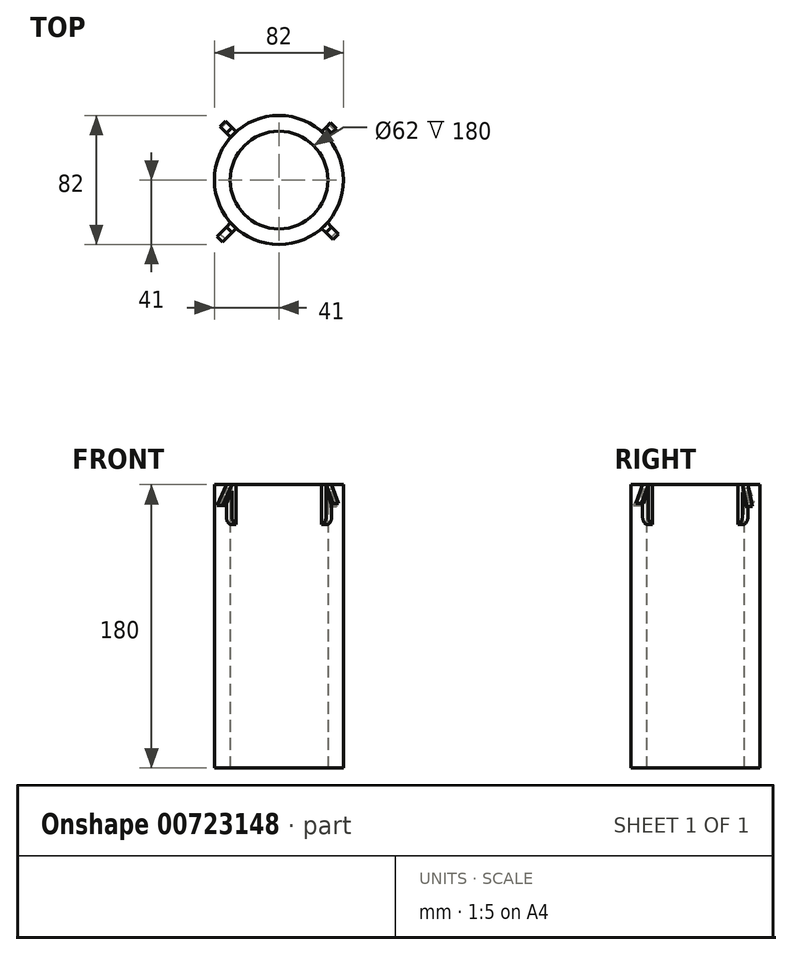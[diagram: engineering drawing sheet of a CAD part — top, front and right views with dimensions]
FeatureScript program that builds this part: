
annotation { "Feature Type Name" : "Feature", "Feature Type Description" : "" }
export const myFeature = defineFeature(function(context is Context, id is Id, definition is map)
    precondition{}
    {
        {
            var Q0;
            Q0=qCreatedBy(makeId("Top.planeOp"),FACE);
            var sketch = newSketch(context, id + "F0", { "sketchPlane" : qUnion([Q0])});
            skCircle(sketch, "E0", {"center": v(0, 0) * mm, "radius": 41 * mm});
            skCircle(sketch, "E1.0", {"center": v(0, 0) * mm, "radius": 31 * mm});
            skSolve(sketch);
        }
        {
            var Q0;
            Q0=makeQuery(id+"F0.imprint","IMPRINT",FACE,{"disambiguationData":[TD([[makeQuery(id+"F0.imprint","IMPRINT",EDGE,{"derivedFrom":sQuery(id+"F0.wireOp",EDGE,"E0")}),1.0]])]});
            extrude(context, id + "F1", {"entities" : qUnion([Q0]), "endBound" : BoundingType.SYMMETRIC, "depth" : 180 * mm, "offsetDistance" : 25.4 * mm});
        }
        {
            var Q0;
            Q0=makeQuery(id+"F1.opExtrude","CAP_FACE",FACE,{"disambiguationData":[OSD([sQuery(id+"F0.wireOp",EDGE,"E0"),sQuery(id+"F0.wireOp",EDGE,"E1.0")])],"isStart":false});
            var sketch = newSketch(context, id + "F2", { "sketchPlane" : qUnion([Q0])});
            skLineSegment(sketch, "E2", {"start": v(0, 77.1) * mm, "end": v(0, -58.5) * mm});
            skLineSegment(sketch, "E3", {"start": v(-76.39, 0) * mm, "end": v(76.39, 0) * mm});
            skLineSegment(sketch, "E4", {"start": v(-30.73, 27.14) * mm, "end": v(-33.43, 29.83) * mm});
            skLineSegment(sketch, "E5", {"start": v(-33.43, 29.83) * mm, "end": v(-31.63, 31.63) * mm});
            skLineSegment(sketch, "E6", {"start": v(-31.63, 31.63) * mm, "end": v(-29.83, 33.43) * mm});
            skLineSegment(sketch, "E7", {"start": v(-29.83, 33.43) * mm, "end": v(-27.14, 30.73) * mm});
            skPoint(sketch, "E8.MirrorCS.end.orphan", {"position": v(68.66, 68.66) * mm});
            skPoint(sketch, "E8.MirrorCS.start.orphan", {"position": v(0, 0) * mm});
            skLineSegment(sketch, "E9.MirrorCS", {"start": v(33.43, 29.83) * mm, "end": v(31.63, 31.63) * mm});
            skLineSegment(sketch, "E10.MirrorCS", {"start": v(30.73, 27.14) * mm, "end": v(33.43, 29.83) * mm});
            skLineSegment(sketch, "E11.MirrorCS", {"start": v(31.63, 31.63) * mm, "end": v(29.83, 33.43) * mm});
            skLineSegment(sketch, "E12.MirrorCS", {"start": v(29.83, 33.43) * mm, "end": v(27.14, 30.73) * mm});
            skLineSegment(sketch, "E13.MirrorCS", {"start": v(-30.73, -27.14) * mm, "end": v(-33.43, -29.83) * mm});
            skLineSegment(sketch, "E14.MirrorCS", {"start": v(-33.43, -29.83) * mm, "end": v(-31.63, -31.63) * mm});
            skLineSegment(sketch, "E15.MirrorCS", {"start": v(-31.63, -31.63) * mm, "end": v(-29.83, -33.43) * mm});
            skLineSegment(sketch, "E16.MirrorCS", {"start": v(-29.83, -33.43) * mm, "end": v(-27.14, -30.73) * mm});
            skLineSegment(sketch, "E17.MirrorCS", {"start": v(29.83, -33.43) * mm, "end": v(27.14, -30.73) * mm});
            skLineSegment(sketch, "E18.MirrorCS", {"start": v(31.63, -31.63) * mm, "end": v(29.83, -33.43) * mm});
            skLineSegment(sketch, "E19.MirrorCS", {"start": v(33.43, -29.83) * mm, "end": v(31.63, -31.63) * mm});
            skLineSegment(sketch, "E20.MirrorCS", {"start": v(30.73, -27.14) * mm, "end": v(33.43, -29.83) * mm});
            skSolve(sketch);
        }
        {
            var Q0;
            {var subQ1=sQuery(id+"F2.wireOp",EDGE,"E4");Q0=makeQuery(id+"F2.imprint","IMPRINT",FACE,{"disambiguationData":[TD([[makeQuery(id+"F2.imprint","IMPRINT",EDGE,{"derivedFrom":subQ1}),-1.0]])]});}
            var Q1;
            Q1=makeQuery(id+"F2.imprint","IMPRINT",FACE,{"disambiguationData":[TD([[makeQuery(id+"F2.imprint","IMPRINT",EDGE,{"derivedFrom":sQuery(id+"F2.wireOp",EDGE,"E9.MirrorCS")}),1.0]])]});
            var Q2;
            {var subQ1=sQuery(id+"F2.wireOp",EDGE,"E17.MirrorCS");Q2=makeQuery(id+"F2.imprint","IMPRINT",FACE,{"disambiguationData":[TD([[makeQuery(id+"F2.imprint","IMPRINT",EDGE,{"derivedFrom":subQ1}),-1.0]])]});}
            var Q3;
            {var subQ1=sQuery(id+"F2.wireOp",EDGE,"E13.MirrorCS");Q3=makeQuery(id+"F2.imprint","IMPRINT",FACE,{"disambiguationData":[TD([[makeQuery(id+"F2.imprint","IMPRINT",EDGE,{"derivedFrom":subQ1}),1.0]])]});}
            extrude(context, id + "F3", {"entities" : qUnion([Q0, Q1, Q2, Q3]), "oppositeDirection" : true, "depth" : 25.4 * mm, "offsetDistance" : 25.4 * mm});
        }
        {
            var Q0;
            Q0=makeQuery(id+"F3.opExtrude","CAP_EDGE",EDGE,{"disambiguationData":[OSD([sQuery(id+"F2.wireOp",EDGE,"E5"),sQuery(id+"F2.wireOp",EDGE,"E6")])],"isStart":false});
            var Q1;
            Q1=makeQuery(id+"F3.opExtrude","CAP_EDGE",EDGE,{"disambiguationData":[OSD([sQuery(id+"F2.wireOp",EDGE,"E14.MirrorCS"),sQuery(id+"F2.wireOp",EDGE,"E15.MirrorCS")])],"isStart":false});
            var Q2;
            Q2=makeQuery(id+"F3.opExtrude","CAP_EDGE",EDGE,{"disambiguationData":[OSD([sQuery(id+"F2.wireOp",EDGE,"E18.MirrorCS"),sQuery(id+"F2.wireOp",EDGE,"E19.MirrorCS")])],"isStart":false});
            var Q3;
            Q3=makeQuery(id+"F3.opExtrude","CAP_EDGE",EDGE,{"disambiguationData":[OSD([sQuery(id+"F2.wireOp",EDGE,"E9.MirrorCS"),sQuery(id+"F2.wireOp",EDGE,"E11.MirrorCS")])],"isStart":false});
            fillet(context, id + "F4", {"entities" : qUnion([Q0, Q1, Q2, Q3]), "radius" : 5.08 * mm, "tangentPropagation" : true, "allowEdgeOverflow" : false});
        }
        {
            var Q0;
            Q0=makeQuery(id+"F3.opExtrude","SWEPT_FACE",FACE,{"disambiguationData":[OSD([sQuery(id+"F2.wireOp",EDGE,"E7")])]});
            var sketch = newSketch(context, id + "F5", { "sketchPlane" : qUnion([Q0])});
            skLineSegment(sketch, "E21", {"start": v(44.73, 90) * mm, "end": v(50.43, 79.02) * mm});
            skLineSegment(sketch, "E22", {"start": v(50.43, 79.02) * mm, "end": v(49.36, 79.02) * mm});
            skLineSegment(sketch, "E23", {"start": v(49.36, 79.02) * mm, "end": v(44.73, 87.94) * mm});
            skSolve(sketch);
        }
        {
            var Q0;
            {var subQ0=sQuery(id+"F5.wireOp",EDGE,"E21");Q0=makeQuery(id+"F5.imprint","IMPRINT",FACE,{"disambiguationData":[TD([[makeQuery(id+"F5.imprint","IMPRINT",EDGE,{"derivedFrom":subQ0}),-1.0]])]});}
            extrude(context, id + "F6", {"entities" : qUnion([Q0]), "operationType" : NewBodyOperationType.ADD, "oppositeDirection" : true, "depth" : 5.08 * mm, "offsetDistance" : 25.4 * mm});
        }
        {
            var Q0;
            Q0=makeQuery(id+"F3.opExtrude","SWEPT_FACE",FACE,{"disambiguationData":[OSD([sQuery(id+"F2.wireOp",EDGE,"E13.MirrorCS")])]});
            var sketch = newSketch(context, id + "F7", { "sketchPlane" : qUnion([Q0])});
            skLineSegment(sketch, "E24", {"start": v(44.73, 90) * mm, "end": v(53.16, 76.66) * mm});
            skLineSegment(sketch, "E25", {"start": v(53.16, 76.66) * mm, "end": v(50.62, 76.66) * mm});
            skLineSegment(sketch, "E26", {"start": v(50.62, 76.66) * mm, "end": v(44.73, 85.98) * mm});
            skSolve(sketch);
        }
        {
            var Q0;
            {var subQ0=sQuery(id+"F7.wireOp",EDGE,"E24");Q0=makeQuery(id+"F7.imprint","IMPRINT",FACE,{"disambiguationData":[TD([[makeQuery(id+"F7.imprint","IMPRINT",EDGE,{"derivedFrom":subQ0}),-1.0]])]});}
            extrude(context, id + "F8", {"entities" : qUnion([Q0]), "operationType" : NewBodyOperationType.ADD, "oppositeDirection" : true, "depth" : 5.08 * mm, "offsetDistance" : 25.4 * mm});
        }
        {
            var Q0;
            Q0=makeQuery(id+"F3.opExtrude","SWEPT_FACE",FACE,{"disambiguationData":[OSD([sQuery(id+"F2.wireOp",EDGE,"E17.MirrorCS")])]});
            var sketch = newSketch(context, id + "F9", { "sketchPlane" : qUnion([Q0])});
            skLineSegment(sketch, "E27", {"start": v(44.73, 90) * mm, "end": v(50.95, 78.2) * mm});
            skLineSegment(sketch, "E28", {"start": v(50.95, 78.2) * mm, "end": v(49.28, 78.2) * mm});
            skLineSegment(sketch, "E29", {"start": v(49.28, 78.2) * mm, "end": v(44.73, 86.82) * mm});
            skSolve(sketch);
        }
        {
            var Q0;
            Q0=makeQuery(id+"F3.opExtrude","SWEPT_FACE",FACE,{"disambiguationData":[OSD([sQuery(id+"F2.wireOp",EDGE,"E10.MirrorCS")])]});
            var sketch = newSketch(context, id + "F10", { "sketchPlane" : qUnion([Q0])});
            skLineSegment(sketch, "E30", {"start": v(44.73, 90) * mm, "end": v(48.9, 76) * mm});
            skLineSegment(sketch, "E31", {"start": v(48.9, 76) * mm, "end": v(47.39, 76) * mm});
            skLineSegment(sketch, "E32", {"start": v(47.39, 76) * mm, "end": v(44.73, 84.9) * mm});
            skSolve(sketch);
        }
        {
            var Q0;
            {var subQ0=sQuery(id+"F9.wireOp",EDGE,"E27");Q0=makeQuery(id+"F9.imprint","IMPRINT",FACE,{"disambiguationData":[TD([[makeQuery(id+"F9.imprint","IMPRINT",EDGE,{"derivedFrom":subQ0}),-1.0]])]});}
            extrude(context, id + "F11", {"entities" : qUnion([Q0]), "oppositeDirection" : true, "depth" : 5.08 * mm, "offsetDistance" : 25.4 * mm});
        }
        {
            var Q0;
            Q0 = qSketchRegion(id + "F10", true);
            var Q1;
            {var subQ0=sQuery(id+"F10.wireOp",EDGE,"E30");Q1=makeQuery(id+"F10.imprint","IMPRINT",FACE,{"disambiguationData":[TD([[makeQuery(id+"F10.imprint","IMPRINT",EDGE,{"derivedFrom":subQ0}),-1.0]])]});}
            extrude(context, id + "F12", {"entities" : qUnion([Q0, Q1]), "operationType" : NewBodyOperationType.ADD, "oppositeDirection" : true, "depth" : 5.08 * mm, "offsetDistance" : 25.4 * mm});
        }
    });
